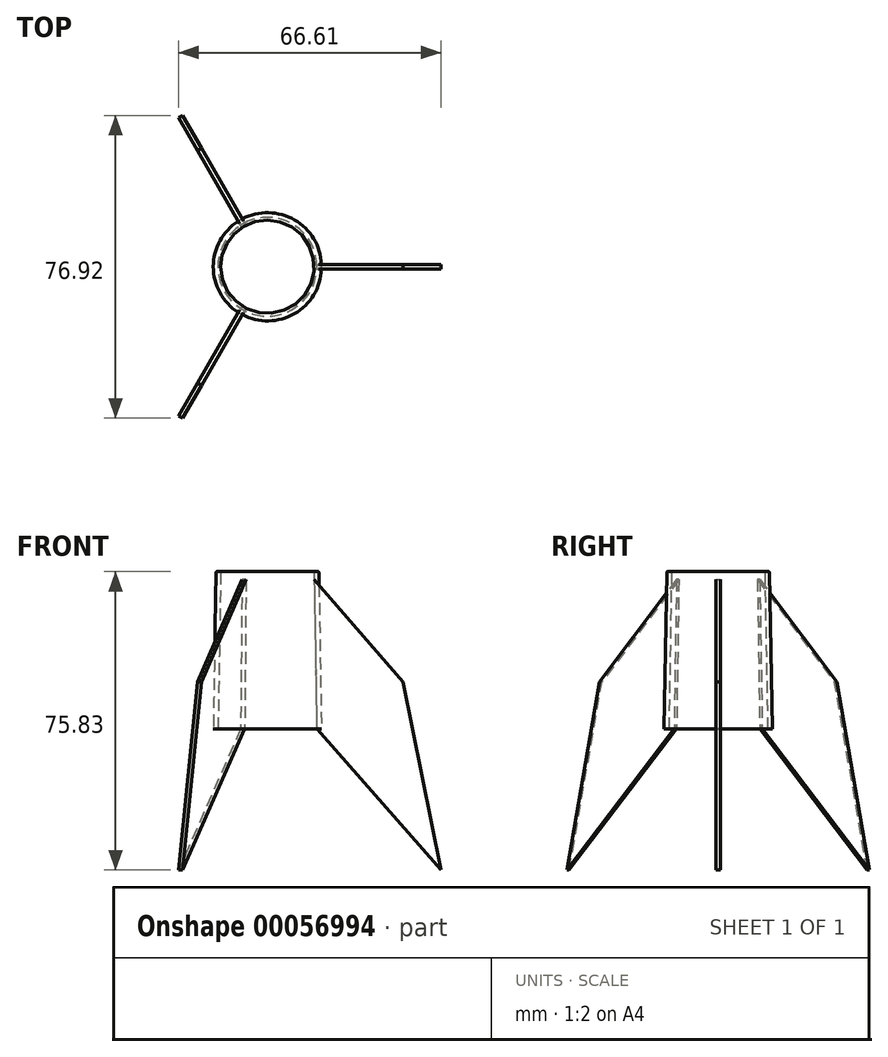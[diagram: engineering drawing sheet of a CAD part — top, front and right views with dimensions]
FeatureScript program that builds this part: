
annotation { "Feature Type Name" : "Feature", "Feature Type Description" : "" }
export const myFeature = defineFeature(function(context is Context, id is Id, definition is map)
    precondition{}
    {
        {
            var Q0;
            Q0=qCreatedBy(makeId("Top.planeOp"),FACE);
            var sketch = newSketch(context, id + "F0", { "sketchPlane" : qUnion([Q0])});
            skCircle(sketch, "E0", {"center": v(0, 0) * mm, "radius": 11.85 * mm});
            skCircle(sketch, "E1", {"center": v(0, 0) * mm, "radius": 12.65 * mm});
            skSolve(sketch);
        }
        {
            var Q0;
            Q0=qCreatedBy(makeId("Front.planeOp"),FACE);
            var sketch = newSketch(context, id + "F1", { "sketchPlane" : qUnion([Q0])});
            skLineSegment(sketch, "E2", {"start": v(0, 0) * mm, "end": v(0, 40) * mm, "construction": true});
            skLineSegment(sketch, "E3.0", {"start": v(-11.85, 0) * mm, "end": v(11.85, 0) * mm, "construction": true});
            skLineSegment(sketch, "E4.0", {"start": v(-12.65, 0) * mm, "end": v(12.65, 0) * mm, "construction": true});
            skLineSegment(sketch, "E5", {"start": v(11.85, 0) * mm, "end": v(11.85, 40) * mm, "construction": true});
            skLineSegment(sketch, "E6", {"start": v(11.85, 39.8) * mm, "end": v(12.55, 0) * mm});
            skLineSegment(sketch, "E7", {"start": v(12.55, 0) * mm, "end": v(13.75, 0.02) * mm});
            skLineSegment(sketch, "E8", {"start": v(13.75, 0.02) * mm, "end": v(13.05, 39.82) * mm});
            skLineSegment(sketch, "E9", {"start": v(12.05, 40) * mm, "end": v(12.85, 40.02) * mm});
            skPoint(sketch, "E10.visualSharp", {"position": v(13.05, 40.02) * mm});
            skArc(sketch, "E10.filletArc", {"start": v(13.05, 39.82) * mm, "mid": v(13, 39.96) * mm, "end": v(12.85, 40.02) * mm});
            skPoint(sketch, "E11.visualSharp", {"position": v(11.85, 40) * mm});
            skArc(sketch, "E11.filletArc", {"start": v(12.05, 40) * mm, "mid": v(11.9, 39.94) * mm, "end": v(11.85, 39.8) * mm});
            skSolve(sketch);
        }
        {
            var Q0;
            Q0=makeQuery(id+"F1.imprint","IMPRINT",FACE,{"disambiguationData":[TD([[makeQuery(id+"F1.imprint","IMPRINT",EDGE,{"derivedFrom":sQuery(id+"F1.wireOp",EDGE,"E6")}),1.0]])]});
            var Q1;
            Q1=sQuery(id+"F1.wireOp",EDGE,"E2");
            revolve(context, id + "F2", {"entities" : qUnion([Q0]), "axis" : qUnion([Q1]), "revolveType" : RevolveType.FULL});
        }
        {
            var Q0;
            Q0=qCreatedBy(makeId("Front.planeOp"),FACE);
            var sketch = newSketch(context, id + "F3", { "sketchPlane" : qUnion([Q0])});
            skLineSegment(sketch, "E12", {"start": v(-13.75, 0.02) * mm, "end": v(-13.05, 39.82) * mm, "construction": true});
            skLineSegment(sketch, "E13", {"start": v(13.05, 39.82) * mm, "end": v(13.75, 0.02) * mm, "construction": true});
            skLineSegment(sketch, "E14", {"start": v(-12.55, 0) * mm, "end": v(-11.85, 39.8) * mm, "construction": true});
            skLineSegment(sketch, "E15", {"start": v(11.88, 38.02) * mm, "end": v(12.55, 0.02) * mm, "construction": true});
            skLineSegment(sketch, "E16", {"start": v(11.88, 38.02) * mm, "end": v(34.48, 12.03) * mm});
            skLineSegment(sketch, "E17", {"start": v(11.88, 38.02) * mm, "end": v(12.55, 0.02) * mm});
            skLineSegment(sketch, "E18", {"start": v(12.55, 0.02) * mm, "end": v(44.06, -35.81) * mm});
            skLineSegment(sketch, "E19", {"start": v(44.06, -35.81) * mm, "end": v(34.48, 12.03) * mm});
            skSolve(sketch);
        }
        {
            var Q0;
            Q0=makeQuery(id+"F3.imprint","IMPRINT",FACE,{"disambiguationData":[TD([[makeQuery(id+"F3.imprint","IMPRINT",EDGE,{"derivedFrom":sQuery(id+"F3.wireOp",EDGE,"E16")}),-1.0]])]});
            extrude(context, id + "F4", {"entities" : qUnion([Q0]), "endBound" : BoundingType.SYMMETRIC, "depth" : 1.2 * mm});
        }
        {
            var Q0;
            Q0=makeQuery(id+"F4.opExtrude","SWEPT_BODY",BODY,{"disambiguationData":[OSD([sQuery(id+"F3.wireOp",EDGE,"E16"),sQuery(id+"F3.wireOp",EDGE,"7tzHYC0D-Ewl8-xDGE-I1kY-fTfFPuimjD0L"),sQuery(id+"F3.wireOp",EDGE,"YT6rEPX3-QJYj-j6T7-dmoI-qzhoSA4LkseR"),sQuery(id+"F3.wireOp",EDGE,"E17")])]});
            var Q1;
            Q1=sQuery(id+"F1.wireOp",EDGE,"E2");
            circularPattern(context, id + "F5", {"entities" : qUnion([Q0]), "axis" : qUnion([Q1]), "angle" : 360 * degree, "instanceCount" : round(3), "equalSpace" : true});
        }
    });
